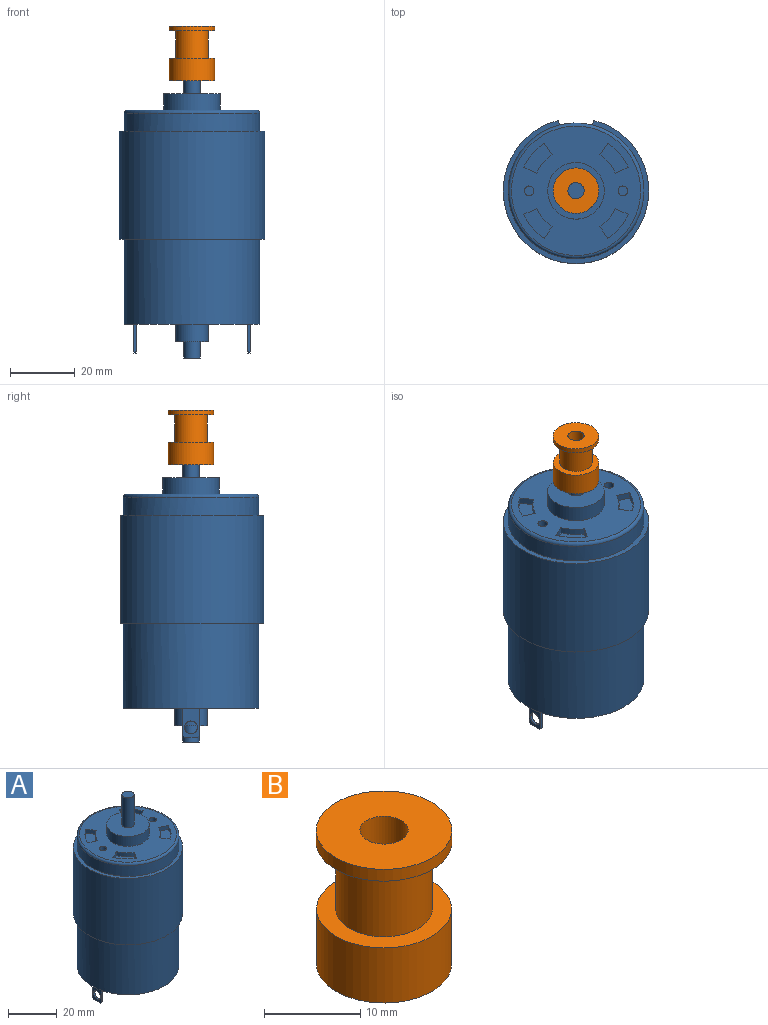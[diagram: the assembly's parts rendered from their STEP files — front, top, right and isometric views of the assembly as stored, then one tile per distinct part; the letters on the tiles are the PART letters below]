
ASSEMBLY  parts=2 mates=1
PART A: 57 faces, bbox 45.5x45.5x96.7 mm
  f0: plane 40x40mm, normal (0,0,1), area 848.8mm2, adj f6,f28,f30,f36,f37,f38,f39,f40
  f1: cylinder r=22.5mm len=45mm, axis (0,0,1), area 4363.7mm2, adj f2,f7,f14,f15
  f2: plane 45x44.32mm, normal (0,0,-1), area 188.9mm2, adj f1,f8,f14,f15
  f3: plane 5x5mm, normal (0,0,1), area 19.6mm2, adj f4
  f4: cylinder r=2.5mm len=15mm, axis (0,0,1), area 235.6mm2, adj f3,f5
  f5: plane 17.5x17.5mm, normal (0,0,1), area 220.9mm2, adj f4,f6
  f6: cylinder r=8.75mm len=17.5mm, axis (0,0,1), area 274.9mm2, adj f0,f5
  f7: plane 45x44.32mm, normal (0,0,1), area 188.9mm2, adj f1,f8,f14,f15
  f8: cylinder r=21mm len=65.2mm, axis (0,0,1), area 4530.2mm2, adj f2,f7,f9,f14,f15,f36
  f9: plane 42x42mm, normal (0,0,-1), area 1299.4mm2, adj f8,f10,f16,f17,f18,f19,f21,f22
  f10: cylinder r=5mm len=10mm, axis (0,0,1), area 172.8mm2, adj f9,f11
  f11: plane 10x10mm, normal (0,0,-1), area 58.9mm2, adj f10,f12
  f12: cylinder r=2.5mm len=5mm, axis (0,0,1), area 78.5mm2, adj f11,f13
  f13: plane 5x5mm, normal (0,0,-1), area 19.6mm2, adj f12
  f14: plane 33.5x1.45mm, normal (-0.97,0.24,0), area 50.3mm2, adj f1,f2,f7,f8
  f15: plane 33.5x1.45mm, normal (0.97,0.24,0), area 50.3mm2, adj f1,f2,f7,f8
  f16: plane 8.5x0.75mm, normal (0,1,0), area 6.4mm2, adj f9,f17,f19,f34
  f17: plane 9x5mm, normal (1,0,0), area 32.2mm2, adj f9,f16,f18,f20,f26,f34,f35
  f18: plane 8.5x0.75mm, normal (0,-1,0), area 6.4mm2, adj f9,f17,f19,f35
  f19: plane 9x5mm, normal (-1,0,0), area 32.2mm2, adj f9,f16,f18,f20,f26,f34,f35
  f20: plane 4x0.75mm, normal (0,0,-1), area 3mm2, adj f17,f19,f34,f35
  f21: plane 8.5x0.75mm, normal (0,1,0), area 6.4mm2, adj f9,f22,f24,f32
  f22: plane 9x5mm, normal (1,0,0), area 32.2mm2, adj f9,f21,f23,f25,f27,f32,f33
  f23: plane 8.5x0.75mm, normal (0,-1,0), area 6.4mm2, adj f9,f22,f24,f33
  f24: plane 9x5mm, normal (-1,0,0), area 32.2mm2, adj f9,f21,f23,f25,f27,f32,f33
  f25: plane 4x0.75mm, normal (0,0,-1), area 3mm2, adj f22,f24,f32,f33
  f26: cylinder r=2mm len=4mm, axis (-1,0,0), area 9.4mm2, adj f17,f19
  f27: cylinder r=2mm len=4mm, axis (1,0,0), area 9.4mm2, adj f22,f24
  f28: cylinder r=1.5mm len=10mm, axis (0,0,1), area 94.2mm2, adj f0,f29
  f29: plane 3x3mm, normal (0,0,1), area 7.1mm2, adj f28
  f30: cylinder r=1.5mm len=10mm, axis (0,0,1), area 94.2mm2, adj f0,f31
  f31: plane 3x3mm, normal (0,0,1), area 7.1mm2, adj f30
  f32: plane 0.75x0.5mm, normal (0,0.71,-0.71), area 0.5mm2, adj f21,f22,f24,f25
  f33: plane 0.75x0.5mm, normal (0,-0.71,-0.71), area 0.5mm2, adj f22,f23,f24,f25
  f34: plane 0.75x0.5mm, normal (0,0.71,-0.71), area 0.5mm2, adj f16,f17,f19,f20
  f35: plane 0.75x0.5mm, normal (0,-0.71,-0.71), area 0.5mm2, adj f17,f18,f19,f20
  f36: torus R=20mm, axis (0,0,1), area 203.7mm2, adj f0,f8
  f37: cylinder r=13.34mm len=5.62mm, axis (0,0,1), area 14.9mm2, adj f0,f38,f40,f41
  f38: plane 4.01x2mm, normal (0.41,-0.91,0), area 8.8mm2, adj f0,f37,f39,f41
  f39: cylinder r=17.74mm len=7.47mm, axis (0,0,1), area 19.9mm2, adj f0,f38,f40,f41
  f40: plane 3.67x2.43mm, normal (-0.83,0.55,0), area 8.8mm2, adj f0,f37,f39,f41
  f41: plane 9.28x8.78mm, normal (0,0,1), area 38.3mm2, adj f37,f38,f39,f40
  f42: cylinder r=13.34mm len=5.62mm, axis (0,0,1), area 14.9mm2, adj f0,f43,f45,f46
  f43: plane 3.67x2.43mm, normal (-0.83,-0.55,0), area 8.8mm2, adj f0,f42,f44,f46
  f44: cylinder r=17.74mm len=7.47mm, axis (0,0,1), area 19.9mm2, adj f0,f43,f45,f46
  f45: plane 4.01x2mm, normal (0.41,0.91,0), area 8.8mm2, adj f0,f42,f44,f46
  f46: plane 9.28x8.78mm, normal (0,0,1), area 38.3mm2, adj f42,f43,f44,f45
  f47: cylinder r=13.34mm len=5.62mm, axis (0,0,1), area 14.9mm2, adj f0,f48,f50,f51
  f48: plane 3.67x2.43mm, normal (0.83,0.55,0), area 8.8mm2, adj f0,f47,f49,f51
  f49: cylinder r=17.74mm len=7.47mm, axis (0,0,1), area 19.9mm2, adj f0,f48,f50,f51
  f50: plane 4.01x2mm, normal (-0.41,-0.91,0), area 8.8mm2, adj f0,f47,f49,f51
  f51: plane 9.28x8.78mm, normal (0,0,1), area 38.3mm2, adj f47,f48,f49,f50
  f52: cylinder r=13.34mm len=5.62mm, axis (0,0,1), area 14.9mm2, adj f0,f53,f55,f56
  f53: plane 4.01x2mm, normal (-0.41,0.91,0), area 8.8mm2, adj f0,f52,f54,f56
  f54: cylinder r=17.74mm len=7.47mm, axis (0,0,1), area 19.9mm2, adj f0,f53,f55,f56
  f55: plane 3.67x2.43mm, normal (0.83,-0.55,0), area 8.8mm2, adj f0,f52,f54,f56
  f56: plane 9.28x8.78mm, normal (0,0,1), area 38.3mm2, adj f52,f53,f54,f55
PART B: 8 faces, bbox 14.1x14.1x17 mm
  f0: cylinder r=2.5mm len=17mm, axis (0,0,-1), area 267mm2, adj f4,f7
  f1: cylinder r=5mm len=10mm, axis (0,0,-1), area 267mm2, adj f3,f5
  f2: cylinder r=7mm len=14mm, axis (0,0,-1), area 307.9mm2, adj f3,f4
  f3: plane 14x14mm, normal (0,0,1), area 75.4mm2, adj f1,f2
  f4: plane 14x14mm, normal (0,0,-1), area 134.3mm2, adj f0,f2
  f5: plane 14.08x14.08mm, normal (0,0,-1), area 77.1mm2, adj f1,f6
  f6: cylinder r=7.04mm len=14.08mm, axis (0,0,1), area 66.3mm2, adj f5,f7
  f7: plane 14.08x14.08mm, normal (0,0,1), area 136mm2, adj f0,f6
PLACE A t=(-0.19,0,-0.08)mm
PLACE B t=(-0.19,0,42.02)mm
MATE fastened A.f1 <-> B.f2  axis (0,0,1) through (-0.19,0,45.52)mm
